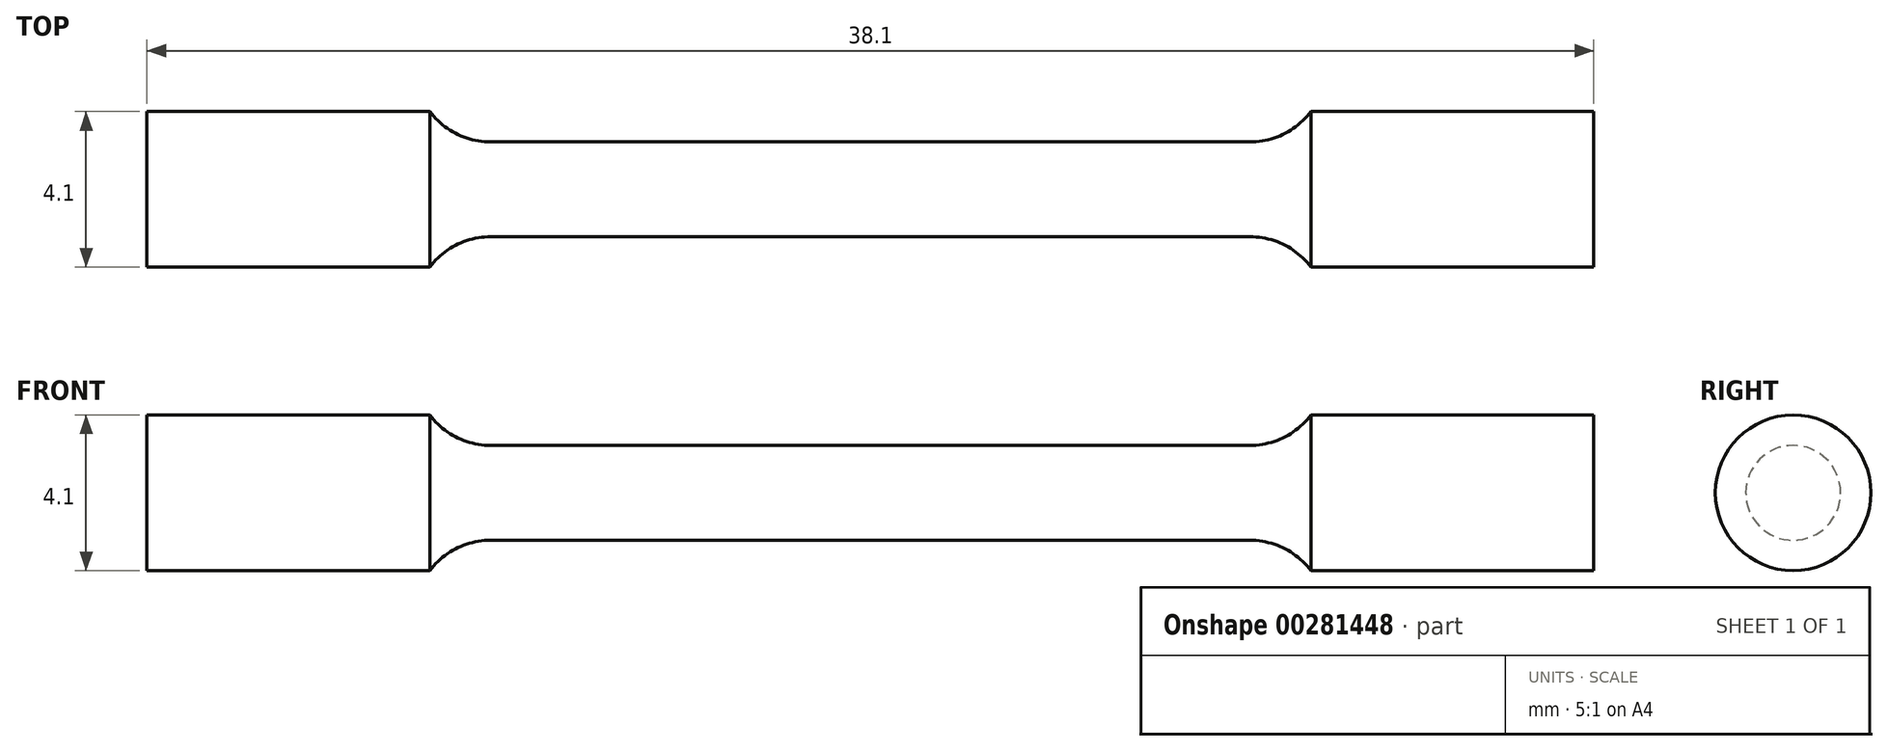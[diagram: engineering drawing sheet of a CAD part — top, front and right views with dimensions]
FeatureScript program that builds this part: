
annotation { "Feature Type Name" : "Feature", "Feature Type Description" : "" }
export const myFeature = defineFeature(function(context is Context, id is Id, definition is map)
    precondition{}
    {
        {
            var Q0;
            Q0=qCreatedBy(makeId("Front.planeOp"),FACE);
            var sketch = newSketch(context, id + "F0", { "sketchPlane" : qUnion([Q0])});
            skLineSegment(sketch, "E0", {"start": v(0, 1.25) * mm, "end": v(10, 1.25) * mm});
            skArc(sketch, "E1", {"start": v(10, 1.25) * mm, "mid": v(10.9, 1.46) * mm, "end": v(11.6, 2.05) * mm});
            skLineSegment(sketch, "E2", {"start": v(11.6, 2.05) * mm, "end": v(19.05, 2.05) * mm});
            skLineSegment(sketch, "E3", {"start": v(19.05, 2.05) * mm, "end": v(19.05, 0) * mm});
            skLineSegment(sketch, "E4.MirrorCS", {"start": v(0, 1.25) * mm, "end": v(-10, 1.25) * mm});
            skArc(sketch, "E5.MirrorCS", {"start": v(-10, 1.25) * mm, "mid": v(-10.9, 1.46) * mm, "end": v(-11.6, 2.05) * mm});
            skLineSegment(sketch, "E6.MirrorCS", {"start": v(-19.05, 2.05) * mm, "end": v(-19.05, 0) * mm});
            skLineSegment(sketch, "E7.MirrorCS", {"start": v(-11.6, 2.05) * mm, "end": v(-19.05, 2.05) * mm});
            skLineSegment(sketch, "E8", {"start": v(-19.05, 0) * mm, "end": v(19.05, 0) * mm});
            skSolve(sketch);
        }
        {
            var Q0;
            Q0 = qSketchRegion(id + "F0", true);
            var Q1;
            Q1=sQuery(id+"F0.wireOp",EDGE,"E8");
            revolve(context, id + "F1", {"entities" : qUnion([Q0]), "axis" : qUnion([Q1]), "revolveType" : RevolveType.FULL});
        }
    });
